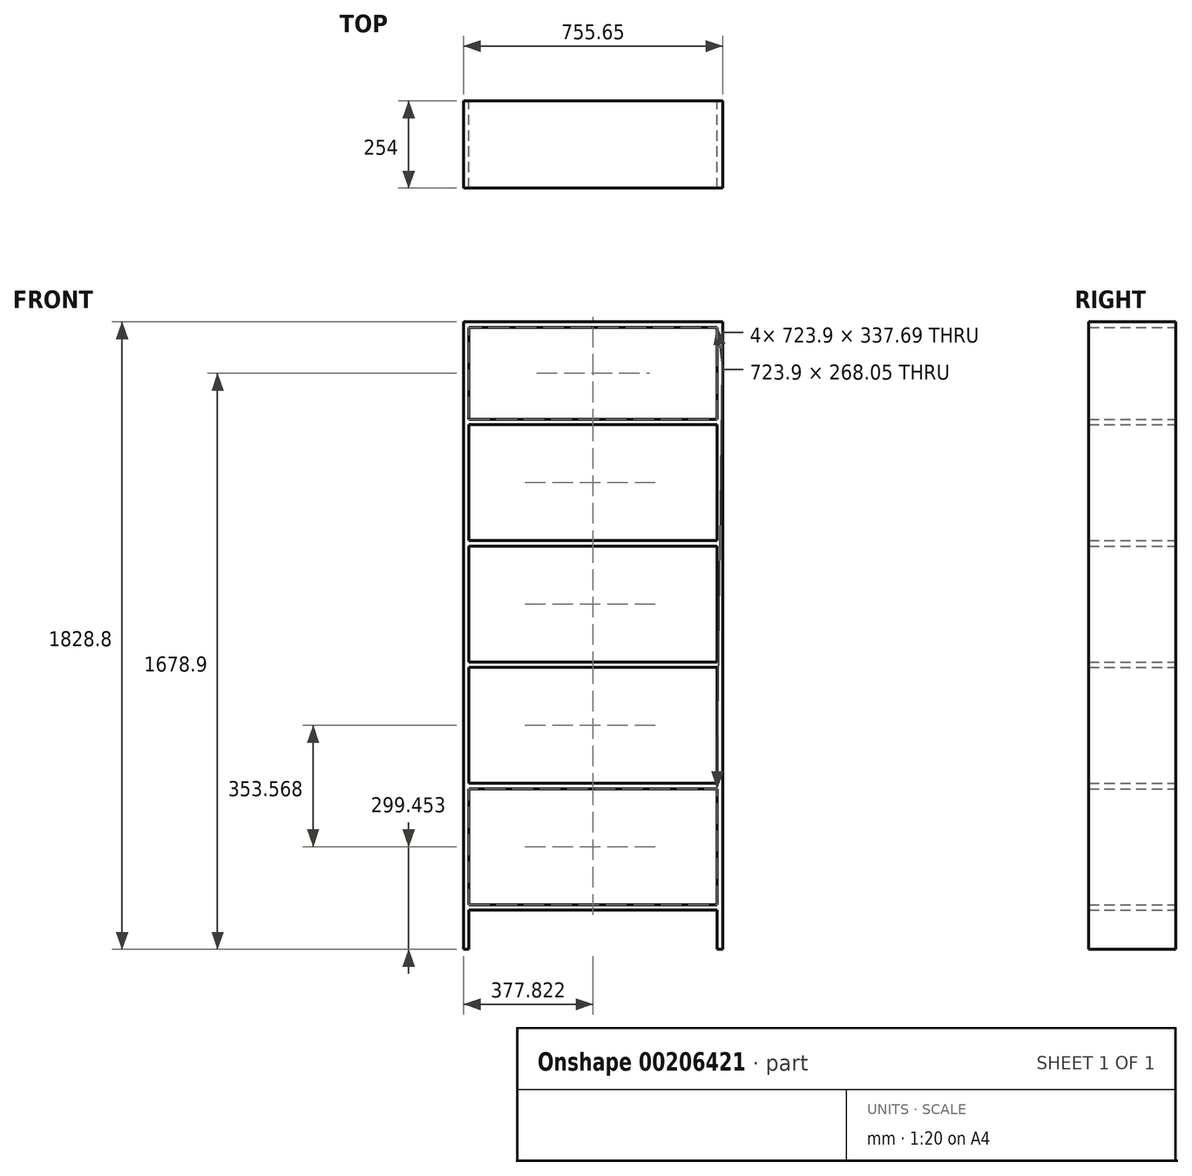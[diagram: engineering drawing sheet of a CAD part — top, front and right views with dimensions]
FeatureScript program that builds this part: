
annotation { "Feature Type Name" : "Feature", "Feature Type Description" : "" }
export const myFeature = defineFeature(function(context is Context, id is Id, definition is map)
    precondition{}
    {
        {
            var Q0;
            Q0=qCreatedBy(makeId("Front.planeOp"),FACE);
            var sketch = newSketch(context, id + "F0", { "sketchPlane" : qUnion([Q0])});
            skLineSegment(sketch, "E0.bottom", {"start": v(563.77, -873.48) * mm, "end": v(547.9, -873.48) * mm});
            skLineSegment(sketch, "E0.top", {"start": v(563.77, 955.32) * mm, "end": v(547.9, 955.32) * mm});
            skLineSegment(sketch, "E0.left", {"start": v(563.77, -873.48) * mm, "end": v(563.77, 955.32) * mm});
            skLineSegment(sketch, "E0.right", {"start": v(547.9, -873.48) * mm, "end": v(547.9, -758.75) * mm});
            skLineSegment(sketch, "E1.bottom", {"start": v(547.9, 955.32) * mm, "end": v(-176, 955.32) * mm});
            skLineSegment(sketch, "E1.top", {"start": v(547.9, 939.45) * mm, "end": v(-176, 939.45) * mm});
            skLineSegment(sketch, "E2.bottom", {"start": v(-176, 955.32) * mm, "end": v(-191.88, 955.32) * mm});
            skLineSegment(sketch, "E2.top", {"start": v(-176, -873.48) * mm, "end": v(-191.88, -873.48) * mm});
            skLineSegment(sketch, "E2.left", {"start": v(-176, 939.45) * mm, "end": v(-176, 671.4) * mm});
            skLineSegment(sketch, "E2.right", {"start": v(-191.88, 955.32) * mm, "end": v(-191.88, -873.48) * mm});
            skLineSegment(sketch, "E3.bottom", {"start": v(-176, -758.75) * mm, "end": v(547.9, -758.75) * mm});
            skLineSegment(sketch, "E3.top", {"start": v(-176, -742.87) * mm, "end": v(547.9, -742.87) * mm});
            skLineSegment(sketch, "E4.0.1.0", {"start": v(-176, -405.18) * mm, "end": v(547.9, -405.18) * mm});
            skLineSegment(sketch, "E4.0.1.1", {"start": v(-176, -389.3) * mm, "end": v(547.9, -389.3) * mm});
            skLineSegment(sketch, "E4.0.2.0", {"start": v(-176, -51.61) * mm, "end": v(547.9, -51.61) * mm});
            skLineSegment(sketch, "E4.0.2.1", {"start": v(-176, -35.74) * mm, "end": v(547.9, -35.74) * mm});
            skLineSegment(sketch, "E4.0.3.0", {"start": v(-176, 301.96) * mm, "end": v(547.9, 301.96) * mm});
            skLineSegment(sketch, "E4.0.3.1", {"start": v(-176, 317.83) * mm, "end": v(547.9, 317.83) * mm});
            skLineSegment(sketch, "E4.0.4.0", {"start": v(-176, 655.52) * mm, "end": v(547.9, 655.52) * mm});
            skLineSegment(sketch, "E4.0.4.1", {"start": v(-176, 671.4) * mm, "end": v(547.9, 671.4) * mm});
            skLineSegment(sketch, "E4.direction1", {"start": v(-176, -758.75) * mm, "end": v(-151, -758.75) * mm, "construction": true});
            skLineSegment(sketch, "E4.direction2", {"start": v(-176, -742.87) * mm, "end": v(-176, -405.18) * mm, "construction": true});
            skLineSegment(sketch, "E5.trimOffspring", {"start": v(547.9, -389.3) * mm, "end": v(547.9, -51.61) * mm});
            skLineSegment(sketch, "E6.trimOffspring", {"start": v(547.9, -742.87) * mm, "end": v(547.9, -405.18) * mm});
            skLineSegment(sketch, "E7.trimOffspring", {"start": v(-176, -758.75) * mm, "end": v(-176, -873.48) * mm});
            skLineSegment(sketch, "E8.trimOffspring", {"start": v(-176, -405.18) * mm, "end": v(-176, -742.87) * mm});
            skLineSegment(sketch, "E9.trimOffspring", {"start": v(-176, -51.61) * mm, "end": v(-176, -389.3) * mm});
            skLineSegment(sketch, "E10.trimOffspring", {"start": v(547.9, -35.74) * mm, "end": v(547.9, 301.96) * mm});
            skLineSegment(sketch, "E11.trimOffspring", {"start": v(547.9, 317.83) * mm, "end": v(547.9, 655.52) * mm});
            skLineSegment(sketch, "E12.trimOffspring", {"start": v(-176, 301.96) * mm, "end": v(-176, -35.74) * mm});
            skLineSegment(sketch, "E13.trimOffspring", {"start": v(547.9, 671.4) * mm, "end": v(547.9, 939.45) * mm});
            skLineSegment(sketch, "E14.trimOffspring", {"start": v(-176, 655.52) * mm, "end": v(-176, 317.83) * mm});
            skSolve(sketch);
        }
        {
            var Q0;
            Q0 = qSketchRegion(id + "F0", true);
            extrude(context, id + "F1", {"entities" : qUnion([Q0]), "depth" : 254 * mm});
        }
    });
